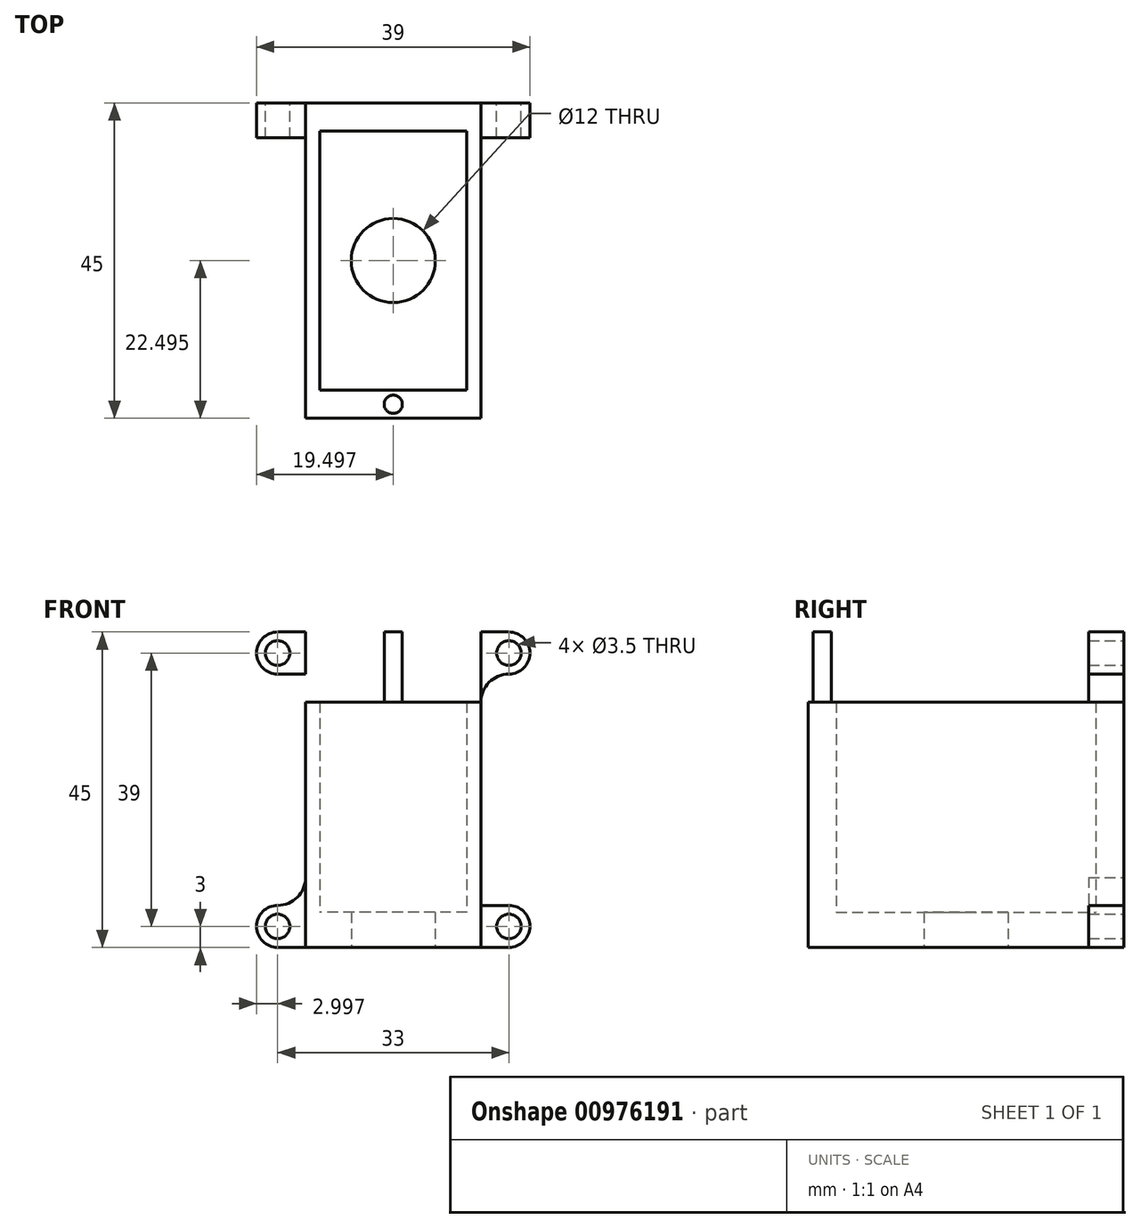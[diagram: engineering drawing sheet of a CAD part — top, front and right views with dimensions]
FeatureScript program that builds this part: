
annotation { "Feature Type Name" : "Feature", "Feature Type Description" : "" }
export const myFeature = defineFeature(function(context is Context, id is Id, definition is map)
    precondition{}
    {
        {
            var Q0;
            Q0=qCreatedBy(makeId("Top.planeOp"),FACE);
            var sketch = newSketch(context, id + "F0", { "sketchPlane" : qUnion([Q0])});
            skLineSegment(sketch, "E0.bottom", {"start": v(-8.88, 12) * mm, "end": v(16.12, 12) * mm});
            skLineSegment(sketch, "E0.top", {"start": v(-8.88, -33) * mm, "end": v(16.12, -33) * mm});
            skLineSegment(sketch, "E0.left", {"start": v(-8.88, 12) * mm, "end": v(-8.88, -33) * mm});
            skLineSegment(sketch, "E0.right", {"start": v(16.12, 12) * mm, "end": v(16.12, -33) * mm});
            skCircle(sketch, "E1", {"center": v(3.62, -10.5) * mm, "radius": 6 * mm});
            skLineSegment(sketch, "E2", {"start": v(-8.88, 8) * mm, "end": v(16.12, 8) * mm});
            skLineSegment(sketch, "E3", {"start": v(-6.88, 8) * mm, "end": v(-6.88, -33) * mm});
            skLineSegment(sketch, "E4", {"start": v(14.12, 8) * mm, "end": v(14.12, -33) * mm});
            skLineSegment(sketch, "E5", {"start": v(-6.88, -29) * mm, "end": v(14.12, -29) * mm});
            skSolve(sketch);
        }
        {
            var Q0;
            Q0=makeQuery(id+"F0.imprint","IMPRINT",FACE,{"disambiguationData":[TD([[makeQuery(id+"F0.imprint","IMPRINT",EDGE,{"derivedFrom":sQuery(id+"F0.wireOp",EDGE,"E1")}),-1.0]])]});
            var Q1;
            {var subQ1=sQuery(id+"F0.wireOp",EDGE,"E0.bottom");Q1=makeQuery(id+"F0.imprint","IMPRINT",FACE,{"disambiguationData":[TD([[makeQuery(id+"F0.imprint","IMPRINT",EDGE,{"derivedFrom":subQ1}),-1.0]])]});}
            var Q2;
            {var subQ4=sQuery(id+"F0.wireOp",EDGE,"E0.left");var subQ5=sQuery(id+"F0.wireOp",EDGE,"E0.top");var subQ6=makeQuery(id+"F0.imprint","INTERSECT",VERTEX,{"derivedFrom":[subQ5,subQ4]});Q2=makeQuery(id+"F0.imprint","IMPRINT",FACE,{"disambiguationData":[TD([[makeQuery(id+"F0.imprint","IMPRINT",EDGE,{"disambiguationData":[TD([[subQ6,-1.0]])],"derivedFrom":subQ5}),1.0]])]});}
            var Q3;
            {var subQ4=sQuery(id+"F0.wireOp",EDGE,"E0.right");var subQ5=sQuery(id+"F0.wireOp",EDGE,"E0.top");var subQ6=makeQuery(id+"F0.imprint","INTERSECT",VERTEX,{"derivedFrom":[subQ5,subQ4]});Q3=makeQuery(id+"F0.imprint","IMPRINT",FACE,{"disambiguationData":[TD([[makeQuery(id+"F0.imprint","IMPRINT",EDGE,{"disambiguationData":[TD([[subQ6,1.0]])],"derivedFrom":subQ5}),1.0]])]});}
            var Q4;
            {var subQ5=sQuery(id+"F0.wireOp",EDGE,"E5");Q4=makeQuery(id+"F0.imprint","IMPRINT",FACE,{"disambiguationData":[TD([[makeQuery(id+"F0.imprint","IMPRINT",EDGE,{"derivedFrom":subQ5}),-1.0]])]});}
            extrude(context, id + "F1", {"entities" : qUnion([Q0, Q1, Q2, Q3, Q4]), "depth" : 5 * mm, "offsetDistance" : 25 * mm});
        }
        {
            var Q0;
            {var subQ1=sQuery(id+"F0.wireOp",EDGE,"E0.bottom");Q0=makeQuery(id+"F0.imprint","IMPRINT",FACE,{"disambiguationData":[TD([[makeQuery(id+"F0.imprint","IMPRINT",EDGE,{"derivedFrom":subQ1}),-1.0]])]});}
            var Q1;
            {var subQ4=sQuery(id+"F0.wireOp",EDGE,"E0.left");var subQ5=sQuery(id+"F0.wireOp",EDGE,"E0.top");var subQ6=makeQuery(id+"F0.imprint","INTERSECT",VERTEX,{"derivedFrom":[subQ5,subQ4]});Q1=makeQuery(id+"F0.imprint","IMPRINT",FACE,{"disambiguationData":[TD([[makeQuery(id+"F0.imprint","IMPRINT",EDGE,{"disambiguationData":[TD([[subQ6,-1.0]])],"derivedFrom":subQ5}),1.0]])]});}
            var Q2;
            {var subQ4=sQuery(id+"F0.wireOp",EDGE,"E0.right");var subQ5=sQuery(id+"F0.wireOp",EDGE,"E0.top");var subQ6=makeQuery(id+"F0.imprint","INTERSECT",VERTEX,{"derivedFrom":[subQ5,subQ4]});Q2=makeQuery(id+"F0.imprint","IMPRINT",FACE,{"disambiguationData":[TD([[makeQuery(id+"F0.imprint","IMPRINT",EDGE,{"disambiguationData":[TD([[subQ6,1.0]])],"derivedFrom":subQ5}),1.0]])]});}
            var Q3;
            {var subQ5=sQuery(id+"F0.wireOp",EDGE,"E5");Q3=makeQuery(id+"F0.imprint","IMPRINT",FACE,{"disambiguationData":[TD([[makeQuery(id+"F0.imprint","IMPRINT",EDGE,{"derivedFrom":subQ5}),-1.0]])]});}
            extrude(context, id + "F2", {"entities" : qUnion([Q0, Q1, Q2, Q3]), "operationType" : NewBodyOperationType.ADD, "depth" : 45 * mm, "offsetDistance" : 25 * mm});
        }
        {
            var Q0;
            {var subQ0=sQuery(id+"F0.wireOp",EDGE,"E0.bottom");Q0=makeQuery(id+"F2.boolean.opBoolean","MERGE",FACE,{"derivedFrom":[makeQuery(id+"F1.opExtrude","SWEPT_FACE",FACE,{"disambiguationData":[OSD([subQ0])]}),makeQuery(id+"F2.opExtrude","SWEPT_FACE",FACE,{"disambiguationData":[OSD([subQ0])]})]});}
            var sketch = newSketch(context, id + "F3", { "sketchPlane" : qUnion([Q0])});
            skLineSegment(sketch, "E6.bottom", {"start": v(-16.12, 45) * mm, "end": v(-20.12, 45) * mm});
            skLineSegment(sketch, "E6.top", {"start": v(-16.12, 39) * mm, "end": v(-20.12, 39) * mm});
            skLineSegment(sketch, "E6.left", {"start": v(-16.12, 45) * mm, "end": v(-16.12, 39) * mm});
            skLineSegment(sketch, "E6.right", {"start": v(-20.12, 45) * mm, "end": v(-20.12, 39) * mm});
            skArc(sketch, "E7", {"start": v(-20.12, 45) * mm, "mid": v(-23.12, 42) * mm, "end": v(-20.12, 39) * mm});
            skCircle(sketch, "E8", {"center": v(-20.12, 42) * mm, "radius": 1.75 * mm});
            skArc(sketch, "E9", {"start": v(-16.12, 35) * mm, "mid": v(-17.29, 37.83) * mm, "end": v(-20.12, 39) * mm});
            skLineSegment(sketch, "E10", {"start": v(-3.62, 45) * mm, "end": v(-3.62, 0) * mm, "construction": true});
            skLineSegment(sketch, "E11", {"start": v(-16.12, 22.5) * mm, "end": v(8.88, 22.5) * mm, "construction": true});
            skArc(sketch, "E12.MirrorCS", {"start": v(8.88, 35) * mm, "mid": v(10.05, 37.83) * mm, "end": v(12.88, 39) * mm});
            skLineSegment(sketch, "E13.MirrorCS", {"start": v(8.88, 39) * mm, "end": v(12.88, 39) * mm});
            skCircle(sketch, "E14.MirrorC", {"center": v(12.88, 42) * mm, "radius": 1.75 * mm});
            skArc(sketch, "E15.MirrorCS", {"start": v(12.88, 45) * mm, "mid": v(15.88, 42) * mm, "end": v(12.88, 39) * mm});
            skLineSegment(sketch, "E16.MirrorCS", {"start": v(8.88, 45) * mm, "end": v(12.88, 45) * mm});
            skLineSegment(sketch, "E17.MirrorCS", {"start": v(8.88, 22.5) * mm, "end": v(-16.12, 22.5) * mm, "construction": true});
            skArc(sketch, "E18.MirrorCS", {"start": v(-16.12, 10) * mm, "mid": v(-17.29, 7.17) * mm, "end": v(-20.12, 6) * mm});
            skLineSegment(sketch, "E19.MirrorCS", {"start": v(-16.12, 6) * mm, "end": v(-20.12, 6) * mm});
            skArc(sketch, "E20.MirrorCS", {"start": v(-20.12, 0) * mm, "mid": v(-23.12, 3) * mm, "end": v(-20.12, 6) * mm});
            skLineSegment(sketch, "E21.MirrorCS", {"start": v(-16.12, 0) * mm, "end": v(-20.12, 0) * mm});
            skCircle(sketch, "E22.MirrorC", {"center": v(-20.12, 3) * mm, "radius": 1.75 * mm});
            skArc(sketch, "E23.MirrorCS", {"start": v(8.88, 10) * mm, "mid": v(10.05, 7.17) * mm, "end": v(12.88, 6) * mm});
            skLineSegment(sketch, "E24.MirrorCS", {"start": v(8.88, 6) * mm, "end": v(12.88, 6) * mm});
            skLineSegment(sketch, "E25.MirrorCS", {"start": v(8.88, 0) * mm, "end": v(12.88, 0) * mm});
            skArc(sketch, "E26.MirrorCS", {"start": v(12.88, 0) * mm, "mid": v(15.88, 3) * mm, "end": v(12.88, 6) * mm});
            skCircle(sketch, "E27.MirrorC", {"center": v(12.88, 3) * mm, "radius": 1.75 * mm});
            skSolve(sketch);
        }
        {
            var Q0;
            {var subQ0=sQuery(id+"F3.wireOp",EDGE,"E6.top");Q0=makeQuery(id+"F3.imprint","IMPRINT",FACE,{"disambiguationData":[TD([[makeQuery(id+"F3.imprint","IMPRINT",EDGE,{"derivedFrom":subQ0}),1.0]])]});}
            var Q1;
            {var subQ2=sQuery(id+"F3.wireOp",EDGE,"E6.bottom");Q1=makeQuery(id+"F3.imprint","IMPRINT",FACE,{"disambiguationData":[TD([[makeQuery(id+"F3.imprint","IMPRINT",EDGE,{"derivedFrom":subQ2}),1.0]])]});}
            var Q2;
            {var subQ0=sQuery(id+"F3.wireOp",EDGE,"E7");Q2=makeQuery(id+"F3.imprint","IMPRINT",FACE,{"disambiguationData":[TD([[makeQuery(id+"F3.imprint","IMPRINT",EDGE,{"derivedFrom":subQ0}),1.0]])]});}
            var Q3;
            {var subQ1=sQuery(id+"F3.wireOp",EDGE,"E13.MirrorCS");Q3=makeQuery(id+"F3.imprint","IMPRINT",FACE,{"disambiguationData":[TD([[makeQuery(id+"F3.imprint","IMPRINT",EDGE,{"derivedFrom":subQ1}),1.0]])]});}
            var Q4;
            {var subQ0=sQuery(id+"F3.wireOp",EDGE,"E12.MirrorCS");Q4=makeQuery(id+"F3.imprint","IMPRINT",FACE,{"disambiguationData":[TD([[makeQuery(id+"F3.imprint","IMPRINT",EDGE,{"derivedFrom":subQ0}),1.0]])]});}
            var Q5;
            {var subQ1=sQuery(id+"F3.wireOp",EDGE,"E24.MirrorCS");Q5=makeQuery(id+"F3.imprint","IMPRINT",FACE,{"disambiguationData":[TD([[makeQuery(id+"F3.imprint","IMPRINT",EDGE,{"derivedFrom":subQ1}),-1.0]])]});}
            var Q6;
            {var subQ0=sQuery(id+"F3.wireOp",EDGE,"E23.MirrorCS");Q6=makeQuery(id+"F3.imprint","IMPRINT",FACE,{"disambiguationData":[TD([[makeQuery(id+"F3.imprint","IMPRINT",EDGE,{"derivedFrom":subQ0}),-1.0]])]});}
            var Q7;
            {var subQ0=sQuery(id+"F3.wireOp",EDGE,"E18.MirrorCS");Q7=makeQuery(id+"F3.imprint","IMPRINT",FACE,{"disambiguationData":[TD([[makeQuery(id+"F3.imprint","IMPRINT",EDGE,{"derivedFrom":subQ0}),1.0]])]});}
            var Q8;
            {var subQ1=sQuery(id+"F3.wireOp",EDGE,"E19.MirrorCS");Q8=makeQuery(id+"F3.imprint","IMPRINT",FACE,{"disambiguationData":[TD([[makeQuery(id+"F3.imprint","IMPRINT",EDGE,{"derivedFrom":subQ1}),1.0]])]});}
            extrude(context, id + "F4", {"entities" : qUnion([Q0, Q1, Q2, Q3, Q4, Q5, Q6, Q7, Q8]), "oppositeDirection" : true, "depth" : 5 * mm, "offsetDistance" : 25 * mm});
        }
        {
            var Q0;
            Q0=makeQuery(id+"F2.opExtrude","CAP_FACE",FACE,{"disambiguationData":[OSD([sQuery(id+"F0.wireOp",EDGE,"E0.bottom"),sQuery(id+"F0.wireOp",EDGE,"E0.top"),sQuery(id+"F0.wireOp",EDGE,"E0.left"),sQuery(id+"F0.wireOp",EDGE,"E0.right"),sQuery(id+"F0.wireOp",EDGE,"E2"),sQuery(id+"F0.wireOp",EDGE,"E3"),sQuery(id+"F0.wireOp",EDGE,"E4"),sQuery(id+"F0.wireOp",EDGE,"E5")])],"isStart":false});
            var sketch = newSketch(context, id + "F5", { "sketchPlane" : qUnion([Q0])});
            skLineSegment(sketch, "E28", {"start": v(3.62, 12) * mm, "end": v(3.62, -33) * mm, "construction": true});
            skLineSegment(sketch, "E29", {"start": v(-8.88, -10.5) * mm, "end": v(16.12, -10.5) * mm, "construction": true});
            skCircle(sketch, "E30", {"center": v(3.62, 10) * mm, "radius": 1.3 * mm});
            skCircle(sketch, "E31.MirrorC", {"center": v(3.62, -31) * mm, "radius": 1.3 * mm});
            skSolve(sketch);
        }
        {
            var Q0;
            Q0=makeQuery(id+"F5.imprint","IMPRINT",FACE,{"disambiguationData":[TD([[makeQuery(id+"F5.imprint","IMPRINT",EDGE,{"derivedFrom":sQuery(id+"F5.wireOp",EDGE,"E30")}),1.0]])]});
            var Q1;
            Q1=makeQuery(id+"F5.imprint","IMPRINT",FACE,{"disambiguationData":[TD([[makeQuery(id+"F5.imprint","IMPRINT",EDGE,{"derivedFrom":sQuery(id+"F5.wireOp",EDGE,"E31.MirrorC")}),-1.0]])]});
            extrude(context, id + "F6", {"entities" : qUnion([Q0, Q1]), "operationType" : NewBodyOperationType.REMOVE, "oppositeDirection" : true, "depth" : 10 * mm, "offsetDistance" : 25 * mm});
        }
    });
